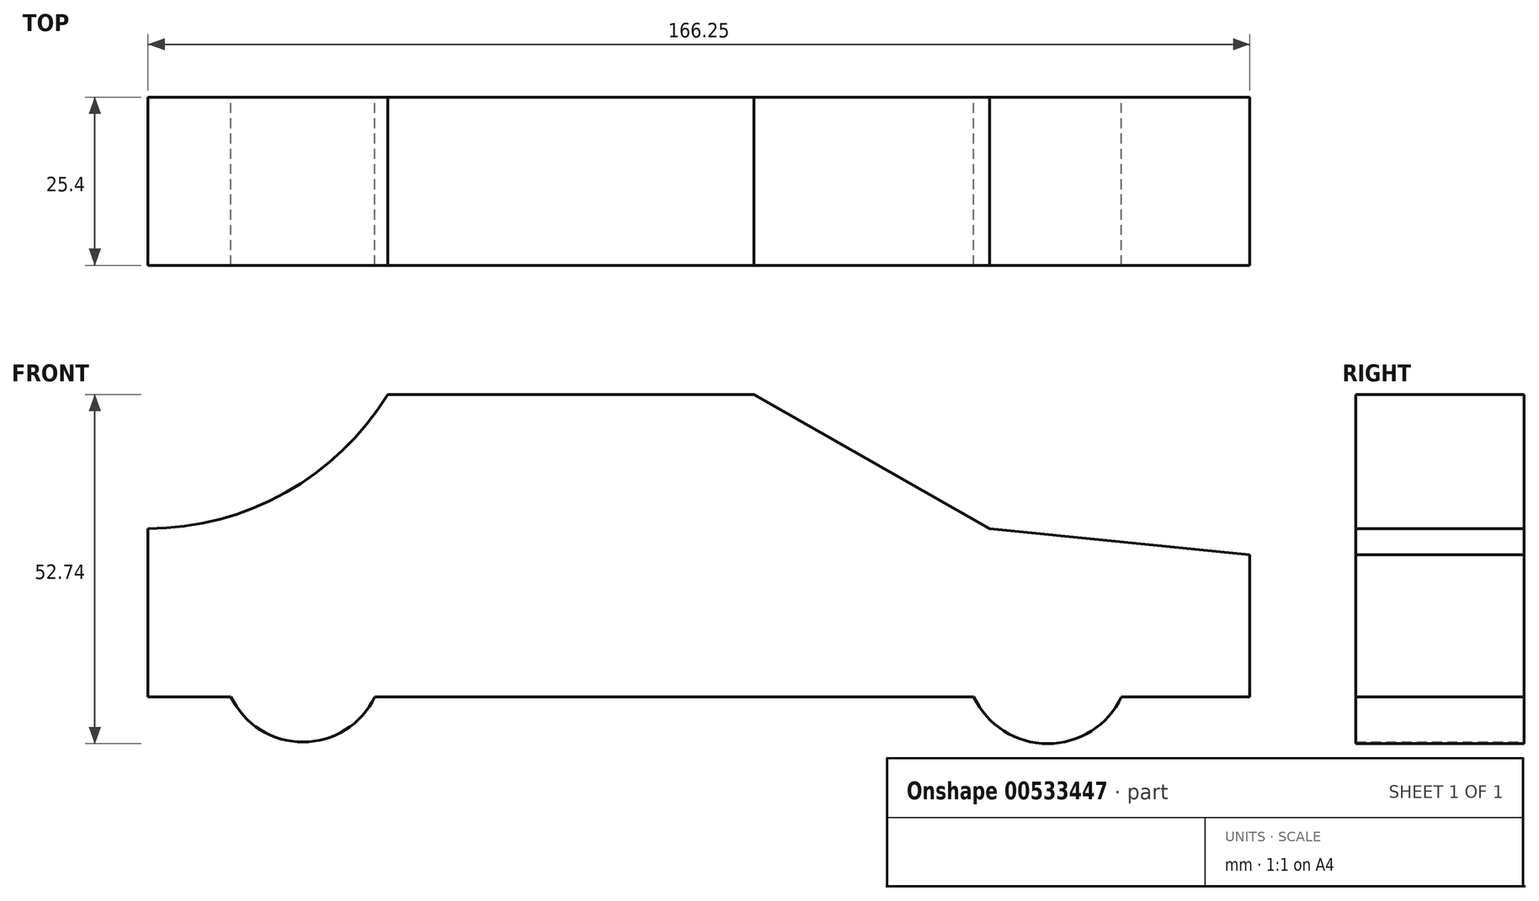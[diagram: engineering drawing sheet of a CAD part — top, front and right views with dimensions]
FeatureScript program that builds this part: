
annotation { "Feature Type Name" : "Feature", "Feature Type Description" : "" }
export const myFeature = defineFeature(function(context is Context, id is Id, definition is map)
    precondition{}
    {
        {
            var Q0;
            Q0=qCreatedBy(makeId("Front.planeOp"),FACE);
            var sketch = newSketch(context, id + "F0", { "sketchPlane" : qUnion([Q0])});
            skLineSegment(sketch, "E0.bottom", {"start": v(-68.86, 44.52) * mm, "end": v(58.14, 44.52) * mm});
            skLineSegment(sketch, "E0.top", {"start": v(-68.86, 19.12) * mm, "end": v(58.14, 19.12) * mm});
            skLineSegment(sketch, "E0.left", {"start": v(-68.86, 44.52) * mm, "end": v(-68.86, 19.12) * mm});
            skLineSegment(sketch, "E0.right", {"start": v(58.14, 44.52) * mm, "end": v(58.14, 19.12) * mm});
            skPoint(sketch, "E1.visualSharp", {"position": v(-68.86, 44.52) * mm});
            skLineSegment(sketch, "E1.filletArc", {"start": v(-68.86, 44.52) * mm, "end": v(-68.86, 44.52) * mm});
            skArc(sketch, "E2", {"start": v(-68.86, 44.52) * mm, "mid": v(-48.14, 49.93) * mm, "end": v(-32.7, 64.77) * mm});
            skLineSegment(sketch, "E3", {"start": v(-32.7, 64.77) * mm, "end": v(22.54, 64.77) * mm});
            skLineSegment(sketch, "E4", {"start": v(22.54, 64.77) * mm, "end": v(58.14, 44.52) * mm});
            skLineSegment(sketch, "E5", {"start": v(58.14, 44.52) * mm, "end": v(97.39, 40.59) * mm});
            skLineSegment(sketch, "E6", {"start": v(58.14, 19.12) * mm, "end": v(97.39, 19.12) * mm});
            skLineSegment(sketch, "E7", {"start": v(97.39, 40.59) * mm, "end": v(97.39, 23.6) * mm});
            skLineSegment(sketch, "E8", {"start": v(97.39, 23.6) * mm, "end": v(97.39, 19.12) * mm});
            skLineSegment(sketch, "E9", {"start": v(97.39, 19.12) * mm, "end": v(97.39, 23.6) * mm});
            skCircle(sketch, "E10", {"center": v(-45.48, 24.32) * mm, "radius": 12.04 * mm});
            skCircle(sketch, "E11", {"center": v(66.88, 24.32) * mm, "radius": 12.3 * mm});
            skSolve(sketch);
        }
        {
            var Q0;
            Q0=makeQuery(id+"F0.imprint","IMPRINT",FACE,{"disambiguationData":[TD([[makeQuery(id+"F0.imprint","IMPRINT",EDGE,{"derivedFrom":sQuery(id+"F0.wireOp",EDGE,"E0.bottom")}),1.0]])]});
            var Q1;
            Q1=makeQuery(id+"F0.imprint","IMPRINT",FACE,{"disambiguationData":[TD([[makeQuery(id+"F0.imprint","IMPRINT",EDGE,{"derivedFrom":sQuery(id+"F0.wireOp",EDGE,"E0.bottom")}),-1.0]])]});
            extrude(context, id + "F1", {"entities" : qUnion([Q0, Q1]), "depth" : 25.4 * mm, "offsetDistance" : 25.4 * mm});
        }
        {
            var Q0;
            Q0 = qSketchRegion(id + "F0", true);
            extrude(context, id + "F2", {"entities" : qUnion([Q0]), "operationType" : NewBodyOperationType.ADD, "depth" : 25.4 * mm, "offsetDistance" : 25.4 * mm});
        }
        {
            var Q0;
            Q0=makeQuery(id+"F0.imprint","IMPRINT",FACE,{"disambiguationData":[TD([[makeQuery(id+"F0.imprint","IMPRINT",EDGE,{"derivedFrom":sQuery(id+"F0.wireOp",EDGE,"E0.right")}),1.0]])]});
            extrude(context, id + "F3", {"entities" : qUnion([Q0]), "operationType" : NewBodyOperationType.ADD, "depth" : 25.4 * mm, "offsetDistance" : 25.4 * mm});
        }
    });
